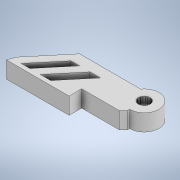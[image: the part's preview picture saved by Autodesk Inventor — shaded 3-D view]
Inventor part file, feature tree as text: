
AUTODESK INVENTOR PART (.ipt)
format: ipt  version: 2021 (Build 250183000, 183)  size: 262,144 bytes
history: native  units: mm
features: extrude x3, sketch x3, other x1, chamfer x1
ambient origin geometry x8: Origin, YZ Plane, XZ Plane, XY Plane, X Axis, Y Axis, Z Axis, Center Point
bodies: Body1 (feature_tree)
feature tree (8):
  other  "Sólido1"
  extrude  "Extrusión1"  Depth=8.0mm TaperAngle=0.0deg
  extrude  "Extrusión6"  Depth=5.0mm
  chamfer  "Chaflán1"  Distance=5.0mm
  extrude  "Extrusión9"  Depth=5.0mm
  sketch  "Boceto1"  dims[d9=0.5mm d10=8.0mm d11=0.0mm]
  sketch  "Boceto6"  dims[d28=5.0mm d29=5.0mm]
  sketch  "Boceto9"  dims[d30=5.0mm d31=5.0mm d32=5.0mm d33=5.0mm d34=5.0mm d35=5.0mm d36=5.0mm d37=10.0mm d38=0.0mm d44=2.0mm d45=2.0mm d46=45.0deg d47=5.2mm d48=2.9mm d49=0.263mm d50=0.526mm d51=0.3mm d52=260.0mm d54=360.0deg d56=2.9mm d57=0.0mm d25=0.5mm d26=0.872665mm d27=0.5mm d39=0.5mm d40=0.872665mm]
